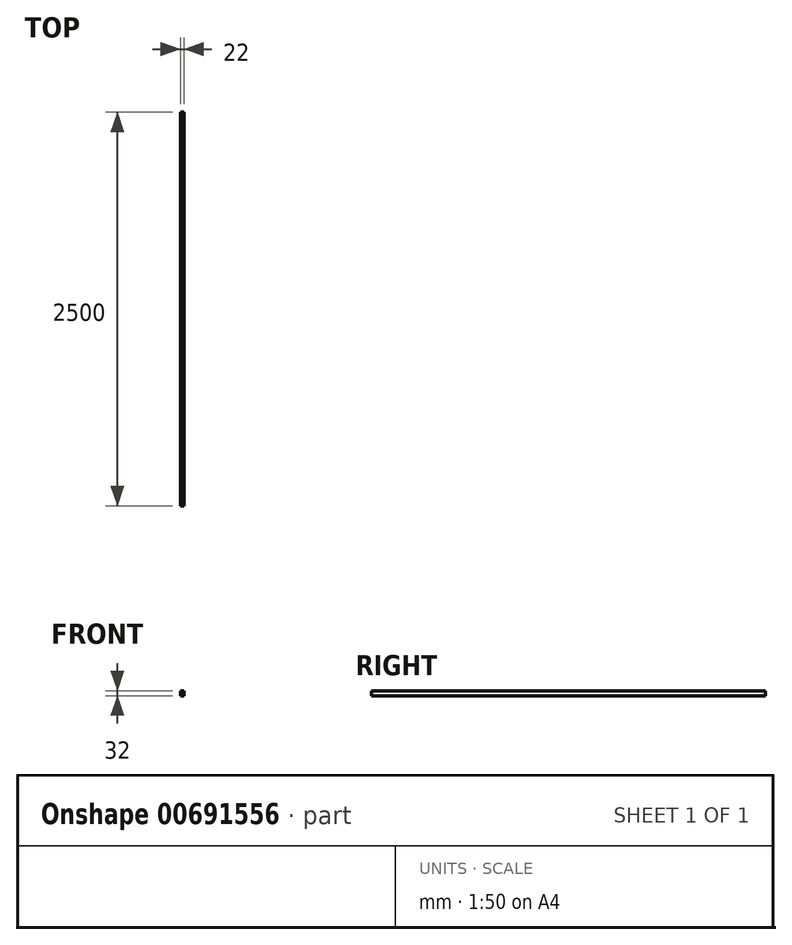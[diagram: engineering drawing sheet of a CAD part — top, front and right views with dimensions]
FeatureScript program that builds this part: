
annotation { "Feature Type Name" : "Feature", "Feature Type Description" : "" }
export const myFeature = defineFeature(function(context is Context, id is Id, definition is map)
    precondition{}
    {
        {
            var Q0;
            Q0=qCreatedBy(makeId("Right.planeOp"),FACE);
            var sketch = newSketch(context, id + "F0", { "sketchPlane" : qUnion([Q0])});
            skLineSegment(sketch, "E0.bottom", {"start": v(1250, -16) * mm, "end": v(-1250, -16) * mm});
            skLineSegment(sketch, "E0.top", {"start": v(1250, 16) * mm, "end": v(-1250, 16) * mm});
            skLineSegment(sketch, "E0.left", {"start": v(1250, -16) * mm, "end": v(1250, 16) * mm});
            skLineSegment(sketch, "E0.right", {"start": v(-1250, -16) * mm, "end": v(-1250, 16) * mm});
            skPoint(sketch, "E0.middle", {"position": v(0, 0) * mm});
            skSolve(sketch);
        }
        {
            var Q0;
            Q0=makeQuery(id+"F0.imprint","IMPRINT",FACE,{"disambiguationData":[TD([[makeQuery(id+"F0.imprint","IMPRINT",EDGE,{"derivedFrom":sQuery(id+"F0.wireOp",EDGE,"E0.bottom")}),-1.0]])]});
            extrude(context, id + "F1", {"entities" : qUnion([Q0]), "endBound" : BoundingType.SYMMETRIC, "depth" : 22 * mm, "offsetDistance" : 25 * mm});
        }
    });
